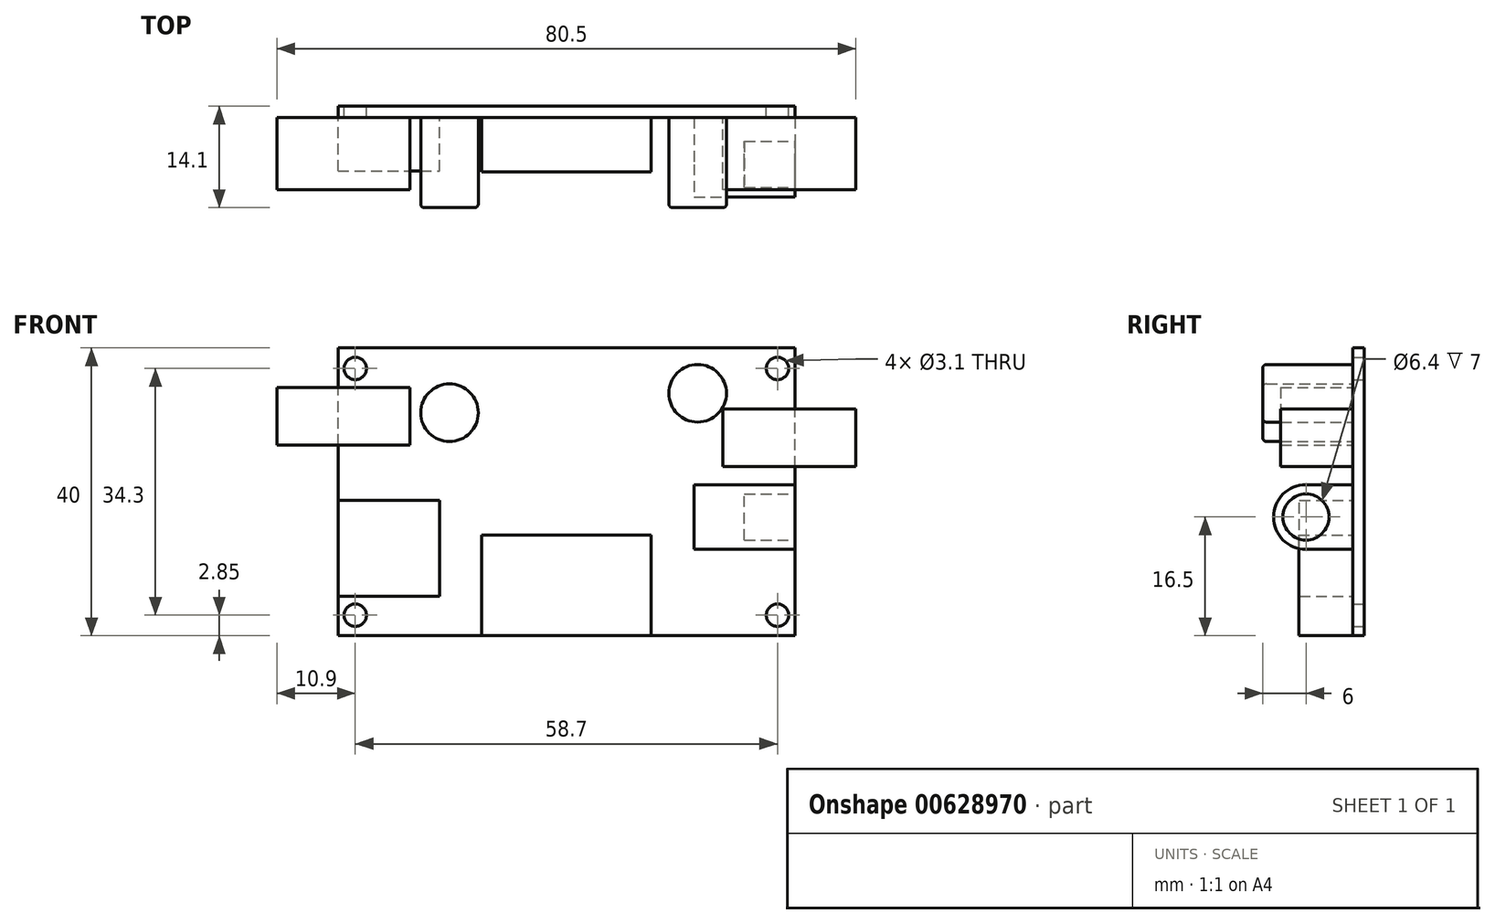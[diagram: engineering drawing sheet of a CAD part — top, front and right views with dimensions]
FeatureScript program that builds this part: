
annotation { "Feature Type Name" : "Feature", "Feature Type Description" : "" }
export const myFeature = defineFeature(function(context is Context, id is Id, definition is map)
    precondition{}
    {
        {
            var Q0;
            Q0=qCreatedBy(makeId("Front.planeOp"),FACE);
            var sketch = newSketch(context, id + "F0", { "sketchPlane" : qUnion([Q0])});
            skLineSegment(sketch, "E0.bottom", {"start": v(31.75, -20) * mm, "end": v(-31.75, -20) * mm});
            skLineSegment(sketch, "E0.top", {"start": v(31.75, 20) * mm, "end": v(-31.75, 20) * mm});
            skLineSegment(sketch, "E0.left", {"start": v(31.75, -20) * mm, "end": v(31.75, 20) * mm});
            skLineSegment(sketch, "E0.right", {"start": v(-31.75, -20) * mm, "end": v(-31.75, 20) * mm});
            skPoint(sketch, "E0.middle", {"position": v(0, 0) * mm});
            skLineSegment(sketch, "E1.bottom", {"start": v(29.35, -17.15) * mm, "end": v(-29.35, -17.15) * mm, "construction": true});
            skLineSegment(sketch, "E1.top", {"start": v(29.35, 17.15) * mm, "end": v(-29.35, 17.15) * mm, "construction": true});
            skLineSegment(sketch, "E1.left", {"start": v(29.35, -17.15) * mm, "end": v(29.35, 17.15) * mm, "construction": true});
            skLineSegment(sketch, "E1.right", {"start": v(-29.35, -17.15) * mm, "end": v(-29.35, 17.15) * mm, "construction": true});
            skSolve(sketch);
        }
        {
            var Q0;
            Q0=makeQuery(id+"F0.imprint","IMPRINT",FACE,{"disambiguationData":[TD([[makeQuery(id+"F0.imprint","IMPRINT",EDGE,{"derivedFrom":sQuery(id+"F0.wireOp",EDGE,"E0.bottom")}),-1.0]])]});
            extrude(context, id + "F1", {"entities" : qUnion([Q0]), "depth" : 1.6 * mm, "offsetDistance" : 25 * mm});
        }
        {
            var Q0;
            Q0=sQuery(id+"F0.wireOp",VERTEX,"E1.right.end");
            var Q1;
            Q1=sQuery(id+"F0.wireOp",VERTEX,"E1.left.end");
            var Q2;
            Q2=sQuery(id+"F0.wireOp",VERTEX,"E1.left.start");
            var Q3;
            Q3=sQuery(id+"F0.wireOp",VERTEX,"E1.right.start");
            var Q4;
            Q4=makeQuery(id+"F1.opExtrude","SWEPT_BODY",BODY,{"disambiguationData":[OSD([sQuery(id+"F0.wireOp",EDGE,"E0.bottom"),sQuery(id+"F0.wireOp",EDGE,"E0.top"),sQuery(id+"F0.wireOp",EDGE,"E0.left"),sQuery(id+"F0.wireOp",EDGE,"E0.right")])]});
            hole(context, id + "F2", {"style" : HoleStyle.SIMPLE, "endStyle" : HoleEndStyle.THROUGH, "oppositeDirection" : true, "holeDiameter" : 3.1 * mm, "majorDiameter" : 5 * mm, "isTappedThrough" : true, "tappedDepth" : 2.3 * mm, "tapClearance" : 3, "startFromSketch" : true, "locations" : qUnion([Q0, Q1, Q2, Q3]), "scope" : qUnion([Q4])});
        }
        {
            var Q0;
            Q0=makeQuery(id+"F1.opExtrude","CAP_FACE",FACE,{"disambiguationData":[OSD([sQuery(id+"F0.wireOp",EDGE,"E0.bottom"),sQuery(id+"F0.wireOp",EDGE,"E0.top"),sQuery(id+"F0.wireOp",EDGE,"E0.left"),sQuery(id+"F0.wireOp",EDGE,"E0.right")])],"isStart":false});
            var sketch = newSketch(context, id + "F3", { "sketchPlane" : qUnion([Q0])});
            skLineSegment(sketch, "E2.bottom", {"start": v(-11.75, -20) * mm, "end": v(11.75, -20) * mm});
            skLineSegment(sketch, "E2.top", {"start": v(-11.75, -6) * mm, "end": v(11.75, -6) * mm});
            skLineSegment(sketch, "E2.left", {"start": v(-11.75, -20) * mm, "end": v(-11.75, -6) * mm});
            skLineSegment(sketch, "E2.right", {"start": v(11.75, -20) * mm, "end": v(11.75, -6) * mm});
            skPoint(sketch, "E2.middle", {"position": v(0, -13) * mm});
            skSolve(sketch);
        }
        {
            var Q0;
            Q0=makeQuery(id+"F3.imprint","IMPRINT",FACE,{"disambiguationData":[TD([[makeQuery(id+"F3.imprint","IMPRINT",EDGE,{"derivedFrom":sQuery(id+"F3.wireOp",EDGE,"E2.bottom")}),-1.0]])]});
            extrude(context, id + "F4", {"entities" : qUnion([Q0]), "depth" : 7.5 * mm, "offsetDistance" : 25 * mm});
        }
        {
            var Q0;
            Q0=makeQuery(id+"F1.opExtrude","CAP_FACE",FACE,{"disambiguationData":[OSD([sQuery(id+"F0.wireOp",EDGE,"E0.bottom"),sQuery(id+"F0.wireOp",EDGE,"E0.top"),sQuery(id+"F0.wireOp",EDGE,"E0.left"),sQuery(id+"F0.wireOp",EDGE,"E0.right")])],"isStart":false});
            var sketch = newSketch(context, id + "F5", { "sketchPlane" : qUnion([Q0])});
            skLineSegment(sketch, "E3.bottom", {"start": v(-31.75, -14.5) * mm, "end": v(-17.65, -14.5) * mm});
            skLineSegment(sketch, "E3.top", {"start": v(-31.75, -1.2) * mm, "end": v(-17.65, -1.2) * mm});
            skLineSegment(sketch, "E3.left", {"start": v(-31.75, -14.5) * mm, "end": v(-31.75, -1.2) * mm});
            skLineSegment(sketch, "E3.right", {"start": v(-17.65, -14.5) * mm, "end": v(-17.65, -1.2) * mm});
            skPoint(sketch, "E3.middle", {"position": v(-24.7, -7.85) * mm});
            skSolve(sketch);
        }
        {
            var Q0;
            Q0=makeQuery(id+"F5.imprint","IMPRINT",FACE,{"disambiguationData":[TD([[makeQuery(id+"F5.imprint","IMPRINT",EDGE,{"derivedFrom":sQuery(id+"F5.wireOp",EDGE,"E3.bottom")}),1.0]])]});
            extrude(context, id + "F6", {"entities" : qUnion([Q0]), "depth" : 7.4 * mm, "offsetDistance" : 25 * mm});
        }
        {
            var Q0;
            Q0=makeQuery(id+"F1.opExtrude","CAP_FACE",FACE,{"disambiguationData":[OSD([sQuery(id+"F0.wireOp",EDGE,"E0.bottom"),sQuery(id+"F0.wireOp",EDGE,"E0.top"),sQuery(id+"F0.wireOp",EDGE,"E0.left"),sQuery(id+"F0.wireOp",EDGE,"E0.right")])],"isStart":false});
            var sketch = newSketch(context, id + "F7", { "sketchPlane" : qUnion([Q0])});
            skLineSegment(sketch, "E4.bottom", {"start": v(-21.75, 14.5) * mm, "end": v(-40.25, 14.5) * mm});
            skLineSegment(sketch, "E4.top", {"start": v(-21.75, 6.5) * mm, "end": v(-40.25, 6.5) * mm});
            skLineSegment(sketch, "E4.left", {"start": v(-21.75, 14.5) * mm, "end": v(-21.75, 6.5) * mm});
            skLineSegment(sketch, "E4.right", {"start": v(-40.25, 14.5) * mm, "end": v(-40.25, 6.5) * mm});
            skPoint(sketch, "E4.middle", {"position": v(-31, 10.5) * mm});
            skLineSegment(sketch, "E5.bottom", {"start": v(40.25, 11.5) * mm, "end": v(21.75, 11.5) * mm});
            skLineSegment(sketch, "E5.top", {"start": v(40.25, 3.5) * mm, "end": v(21.75, 3.5) * mm});
            skLineSegment(sketch, "E5.left", {"start": v(40.25, 11.5) * mm, "end": v(40.25, 3.5) * mm});
            skLineSegment(sketch, "E5.right", {"start": v(21.75, 11.5) * mm, "end": v(21.75, 3.5) * mm});
            skPoint(sketch, "E5.middle", {"position": v(31, 7.5) * mm});
            skSolve(sketch);
        }
        {
            var Q0;
            Q0 = qSketchRegion(id + "F7", true);
            extrude(context, id + "F8", {"entities" : qUnion([Q0]), "depth" : 10 * mm, "offsetDistance" : 25 * mm});
        }
        {
            var Q0;
            Q0=makeQuery(id+"F1.opExtrude","CAP_FACE",FACE,{"disambiguationData":[OSD([sQuery(id+"F0.wireOp",EDGE,"E0.bottom"),sQuery(id+"F0.wireOp",EDGE,"E0.top"),sQuery(id+"F0.wireOp",EDGE,"E0.left"),sQuery(id+"F0.wireOp",EDGE,"E0.right")])],"isStart":false});
            var sketch = newSketch(context, id + "F9", { "sketchPlane" : qUnion([Q0])});
            skCircle(sketch, "E6", {"center": v(-16.25, 11) * mm, "radius": 4 * mm});
            skCircle(sketch, "E7", {"center": v(18.25, 13.7) * mm, "radius": 4 * mm});
            skSolve(sketch);
        }
        {
            var Q0;
            Q0=makeQuery(id+"F9.imprint","IMPRINT",FACE,{"disambiguationData":[TD([[makeQuery(id+"F9.imprint","IMPRINT",EDGE,{"derivedFrom":sQuery(id+"F9.wireOp",EDGE,"E6")}),1.0]])]});
            var Q1;
            Q1=makeQuery(id+"F9.imprint","IMPRINT",FACE,{"disambiguationData":[TD([[makeQuery(id+"F9.imprint","IMPRINT",EDGE,{"derivedFrom":sQuery(id+"F9.wireOp",EDGE,"E7")}),1.0]])]});
            extrude(context, id + "F10", {"entities" : qUnion([Q0, Q1]), "depth" : 12.5 * mm, "offsetDistance" : 25 * mm});
        }
        {
            var Q0;
            Q0=makeQuery(id+"F10.opExtrude","CAP_EDGE",EDGE,{"disambiguationData":[OSD([sQuery(id+"F9.wireOp",EDGE,"E6")])],"isStart":false});
            var Q1;
            Q1=makeQuery(id+"F10.opExtrude","CAP_EDGE",EDGE,{"disambiguationData":[OSD([sQuery(id+"F9.wireOp",EDGE,"E7")])],"isStart":false});
            fillet(context, id + "F11", {"entities" : qUnion([Q0, Q1]), "radius" : 0.5 * mm, "tangentPropagation" : true, "allowEdgeOverflow" : false});
        }
        {
            var Q0;
            Q0=makeQuery(id+"F1.opExtrude","SWEPT_FACE",FACE,{"disambiguationData":[OSD([sQuery(id+"F0.wireOp",EDGE,"E0.left")])]});
            var sketch = newSketch(context, id + "F12", { "sketchPlane" : qUnion([Q0])});
            skLineSegment(sketch, "E8.bottom", {"start": v(-1.6, -8) * mm, "end": v(-8.1, -8) * mm});
            skLineSegment(sketch, "E8.top", {"start": v(-1.6, 1) * mm, "end": v(-8.1, 1) * mm});
            skLineSegment(sketch, "E8.left", {"start": v(-1.6, -8) * mm, "end": v(-1.6, 1) * mm});
            skPoint(sketch, "E8.middle", {"position": v(-4.85, -3.5) * mm});
            skArc(sketch, "E9", {"start": v(-8.1, 1) * mm, "mid": v(-12.6, -3.5) * mm, "end": v(-8.1, -8) * mm});
            skCircle(sketch, "E10", {"center": v(-8.1, -3.5) * mm, "radius": 3.2 * mm});
            skSolve(sketch);
        }
        {
            var Q0;
            Q0=makeQuery(id+"F12.imprint","IMPRINT",FACE,{"disambiguationData":[TD([[makeQuery(id+"F12.imprint","IMPRINT",EDGE,{"derivedFrom":sQuery(id+"F12.wireOp",EDGE,"E8.bottom")}),-1.0]])]});
            var Q1;
            Q1=makeQuery(id+"F12.imprint","IMPRINT",FACE,{"disambiguationData":[TD([[makeQuery(id+"F12.imprint","IMPRINT",EDGE,{"derivedFrom":sQuery(id+"F12.wireOp",EDGE,"E10")}),1.0]])]});
            extrude(context, id + "F13", {"entities" : qUnion([Q0, Q1]), "oppositeDirection" : true, "depth" : 14 * mm, "offsetDistance" : 25 * mm});
        }
        {
            var Q0;
            Q0=makeQuery(id+"F12.imprint","IMPRINT",FACE,{"disambiguationData":[TD([[makeQuery(id+"F12.imprint","IMPRINT",EDGE,{"derivedFrom":sQuery(id+"F12.wireOp",EDGE,"E10")}),1.0]])]});
            extrude(context, id + "F14", {"entities" : qUnion([Q0]), "operationType" : NewBodyOperationType.REMOVE, "oppositeDirection" : true, "depth" : 7 * mm, "offsetDistance" : 25 * mm});
        }
    });
